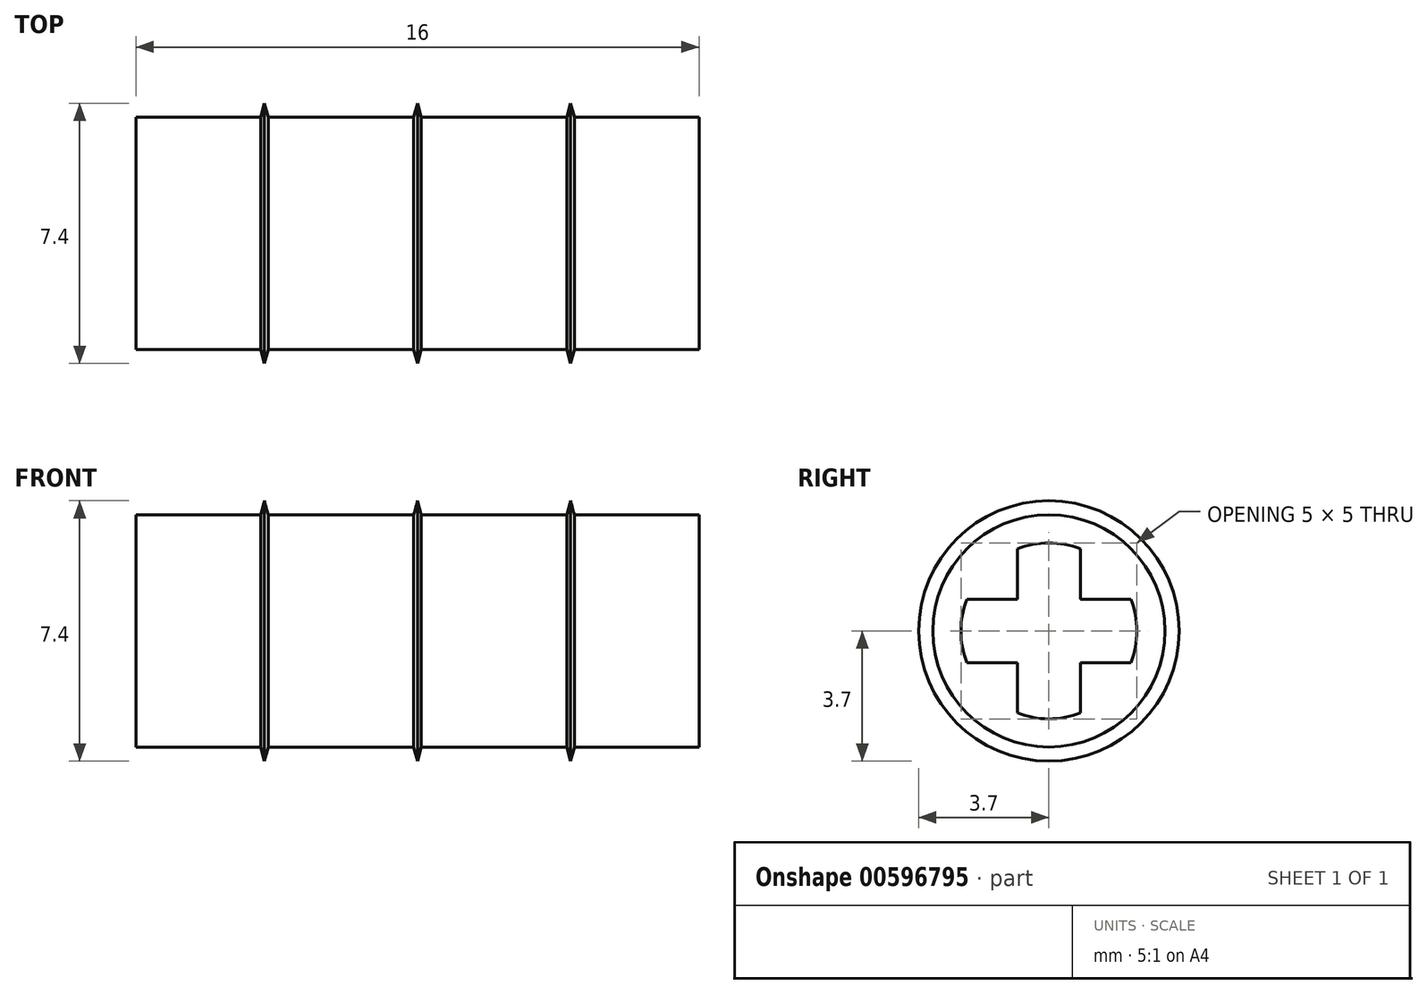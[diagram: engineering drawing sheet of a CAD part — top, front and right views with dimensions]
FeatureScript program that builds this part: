
annotation { "Feature Type Name" : "Feature", "Feature Type Description" : "" }
export const myFeature = defineFeature(function(context is Context, id is Id, definition is map)
    precondition{}
    {
        {
            var Q0;
            Q0=qCreatedBy(makeId("Front.planeOp"),FACE);
            var sketch = newSketch(context, id + "F0", { "sketchPlane" : qUnion([Q0])});
            skLineSegment(sketch, "E0.bottom", {"start": v(8, 3.3) * mm, "end": v(4.46, 3.3) * mm});
            skLineSegment(sketch, "E0.left", {"start": v(8, 3.3) * mm, "end": v(8, 0) * mm});
            skLineSegment(sketch, "E0.right", {"start": v(-8, 3.3) * mm, "end": v(-8, 0) * mm});
            skPoint(sketch, "E0.middle", {"position": v(0, 0) * mm});
            skLineSegment(sketch, "E1.bottom", {"start": v(8, 3.7) * mm, "end": v(-8, 3.7) * mm, "construction": true});
            skLineSegment(sketch, "E1.left", {"start": v(8, 3.7) * mm, "end": v(8, 0) * mm, "construction": true});
            skLineSegment(sketch, "E1.right", {"start": v(-8, 3.7) * mm, "end": v(-8, 3.3) * mm, "construction": true});
            skLineSegment(sketch, "E2", {"start": v(-11.78, 0) * mm, "end": v(11.7, 0) * mm, "construction": true});
            skLineSegment(sketch, "E3.trimOffspring", {"start": v(8, -3.3) * mm, "end": v(8, -3.7) * mm, "construction": true});
            skLineSegment(sketch, "E4.trimOffspring", {"start": v(-8, -3.3) * mm, "end": v(-8, -3.7) * mm, "construction": true});
            skLineSegment(sketch, "E5", {"start": v(-8, 0) * mm, "end": v(8, 0) * mm});
            skLineSegment(sketch, "E6", {"start": v(-4.35, 3.7) * mm, "end": v(-4.46, 3.3) * mm});
            skLineSegment(sketch, "E7", {"start": v(-4.35, 3.7) * mm, "end": v(-4.24, 3.3) * mm});
            skLineSegment(sketch, "E8", {"start": v(4.35, 3.7) * mm, "end": v(4.24, 3.3) * mm});
            skLineSegment(sketch, "E9", {"start": v(4.35, 3.7) * mm, "end": v(4.46, 3.3) * mm});
            skLineSegment(sketch, "E10.trimOffspring", {"start": v(-4.46, 3.3) * mm, "end": v(-8, 3.3) * mm});
            skPoint(sketch, "E11.start.orphan", {"position": v(-4.35, 3.3) * mm});
            skPoint(sketch, "E12.start.orphan", {"position": v(4.35, 3.3) * mm});
            skLineSegment(sketch, "E13.trimOffspring", {"start": v(4.24, 3.3) * mm, "end": v(0.1, 3.3) * mm});
            skLineSegment(sketch, "E14", {"start": v(0, 3.7) * mm, "end": v(-0.1, 3.3) * mm});
            skLineSegment(sketch, "E15", {"start": v(0, 3.7) * mm, "end": v(0.1, 3.3) * mm});
            skLineSegment(sketch, "E16.trimOffspring", {"start": v(-0.1, 3.3) * mm, "end": v(-4.24, 3.3) * mm});
            skPoint(sketch, "E17.orphan", {"position": v(0, 3.3) * mm});
            skSolve(sketch);
        }
        {
            var Q0;
            Q0=makeQuery(id+"F0.imprint","IMPRINT",FACE,{"disambiguationData":[TD([[makeQuery(id+"F0.imprint","IMPRINT",EDGE,{"derivedFrom":sQuery(id+"F0.wireOp",EDGE,"E0.bottom")}),1.0]])]});
            var Q1;
            Q1=sQuery(id+"F0.wireOp",EDGE,"E2");
            revolve(context, id + "F1", {"entities" : qUnion([Q0]), "axis" : qUnion([Q1]), "revolveType" : RevolveType.FULL});
        }
        {
            var Q0;
            Q0=makeQuery(id+"F1.opRevolve","SWEPT_FACE",FACE,{"disambiguationData":[OSD([sQuery(id+"F0.wireOp",EDGE,"E0.right")])]});
            var sketch = newSketch(context, id + "F2", { "sketchPlane" : qUnion([Q0])});
            skCircle(sketch, "E18", {"center": v(0, 0) * mm, "radius": 2.5 * mm});
            skLineSegment(sketch, "E19", {"start": v(0, 0) * mm, "end": v(0, 0.9) * mm, "construction": true});
            skLineSegment(sketch, "E20", {"start": v(0, 0.9) * mm, "end": v(0, -0.9) * mm, "construction": true});
            skPoint(sketch, "E20.endSnap0", {"position": v(0, 0.45) * mm});
            skLineSegment(sketch, "E21", {"start": v(0, 0) * mm, "end": v(0.9, 0) * mm, "construction": true});
            skLineSegment(sketch, "E22", {"start": v(0.9, 0) * mm, "end": v(-0.9, 0) * mm, "construction": true});
            skLineSegment(sketch, "E23", {"start": v(-0.9, 2.33) * mm, "end": v(-0.9, 0.9) * mm});
            skLineSegment(sketch, "E24", {"start": v(-0.9, 0.9) * mm, "end": v(-2.33, 0.9) * mm});
            skLineSegment(sketch, "E25", {"start": v(-0.9, -2.33) * mm, "end": v(-0.9, -0.9) * mm});
            skLineSegment(sketch, "E26", {"start": v(-0.9, -0.9) * mm, "end": v(-2.33, -0.9) * mm});
            skLineSegment(sketch, "E27", {"start": v(0.9, -2.33) * mm, "end": v(0.9, -0.9) * mm});
            skLineSegment(sketch, "E28", {"start": v(0.9, -0.9) * mm, "end": v(2.33, -0.9) * mm});
            skLineSegment(sketch, "E29", {"start": v(0.9, 2.33) * mm, "end": v(0.9, 0.9) * mm});
            skLineSegment(sketch, "E30", {"start": v(0.9, 0.9) * mm, "end": v(2.33, 0.9) * mm});
            skSolve(sketch);
        }
        {
            var Q0;
            {var subQ4=sQuery(id+"F2.wireOp",EDGE,"E23");Q0=makeQuery(id+"F2.imprint","IMPRINT",FACE,{"disambiguationData":[TD([[makeQuery(id+"F2.imprint","IMPRINT",EDGE,{"derivedFrom":subQ4}),1.0]])]});}
            extrude(context, id + "F3", {"entities" : qUnion([Q0]), "operationType" : NewBodyOperationType.REMOVE, "endBound" : BoundingType.THROUGH_ALL, "oppositeDirection" : true, "depth" : 25 * mm, "offsetDistance" : 25 * mm});
        }
    });
